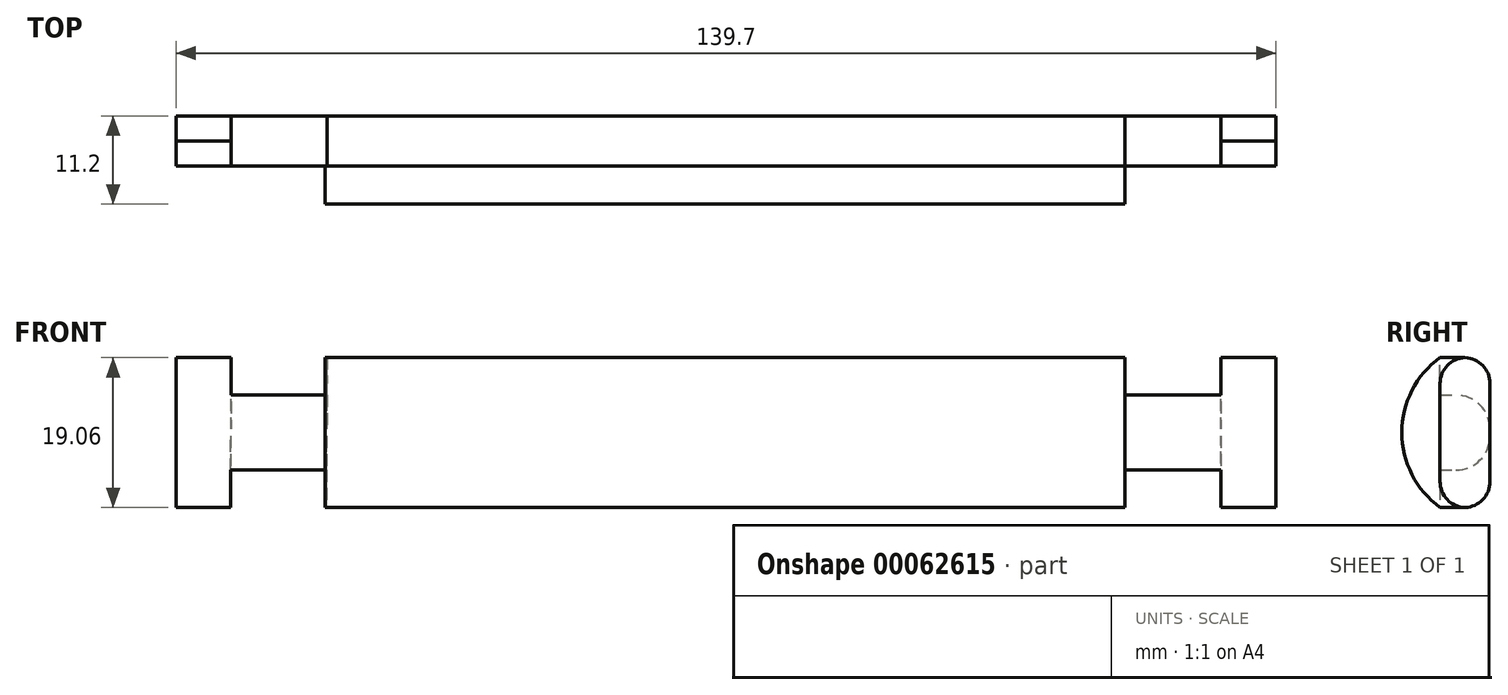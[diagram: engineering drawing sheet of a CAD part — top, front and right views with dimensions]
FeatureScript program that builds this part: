
annotation { "Feature Type Name" : "Feature", "Feature Type Description" : "" }
export const myFeature = defineFeature(function(context is Context, id is Id, definition is map)
    precondition{}
    {
        {
            var Q0;
            Q0=qCreatedBy(makeId("Front.planeOp"),FACE);
            var sketch = newSketch(context, id + "F0", { "sketchPlane" : qUnion([Q0])});
            skLineSegment(sketch, "E0.rect.bottom", {"start": v(69.85, 9.53) * mm, "end": v(-69.85, 9.53) * mm});
            skLineSegment(sketch, "E0.rect.top", {"start": v(69.85, -9.53) * mm, "end": v(-69.85, -9.53) * mm});
            skLineSegment(sketch, "E0.rect.left", {"start": v(69.85, 9.53) * mm, "end": v(69.85, -9.53) * mm});
            skLineSegment(sketch, "E0.rect.right", {"start": v(-69.85, 9.53) * mm, "end": v(-69.85, -9.53) * mm});
            skPoint(sketch, "E0.rect.middle", {"position": v(0, 0) * mm});
            skLineSegment(sketch, "E1", {"start": v(-62.88, 9.53) * mm, "end": v(-62.88, 4.76) * mm});
            skLineSegment(sketch, "E2", {"start": v(-62.88, 4.76) * mm, "end": v(-50.69, 4.76) * mm});
            skLineSegment(sketch, "E3", {"start": v(-50.69, 4.76) * mm, "end": v(-50.69, 9.53) * mm});
            skLineSegment(sketch, "E4", {"start": v(-62.92, -4.76) * mm, "end": v(-62.92, -9.53) * mm});
            skLineSegment(sketch, "E5", {"start": v(-62.92, -4.76) * mm, "end": v(-50.73, -4.76) * mm});
            skLineSegment(sketch, "E6", {"start": v(-50.73, -4.76) * mm, "end": v(-50.73, -9.53) * mm});
            skLineSegment(sketch, "E7", {"start": v(62.9, 9.53) * mm, "end": v(62.9, 4.76) * mm});
            skLineSegment(sketch, "E8", {"start": v(62.9, 4.76) * mm, "end": v(50.7, 4.76) * mm});
            skLineSegment(sketch, "E9", {"start": v(50.7, 4.76) * mm, "end": v(50.7, 9.53) * mm});
            skLineSegment(sketch, "E10", {"start": v(62.9, -9.53) * mm, "end": v(62.9, -4.76) * mm});
            skLineSegment(sketch, "E11", {"start": v(62.9, -4.76) * mm, "end": v(50.7, -4.76) * mm});
            skLineSegment(sketch, "E12", {"start": v(50.7, -4.76) * mm, "end": v(50.7, -9.53) * mm});
            skLineSegment(sketch, "E13", {"start": v(-62.88, 4.76) * mm, "end": v(-62.92, -4.76) * mm, "construction": true});
            skLineSegment(sketch, "E14", {"start": v(62.9, 4.76) * mm, "end": v(62.9, -4.76) * mm, "construction": true});
            skSolve(sketch);
        }
        {
            var Q0;
            {var subQ3=sQuery(id+"F0.wireOp",EDGE,"E0.rect.left");Q0=makeQuery(id+"F0.imprint","IMPRINT",FACE,{"disambiguationData":[TD([[makeQuery(id+"F0.imprint","IMPRINT",EDGE,{"derivedFrom":subQ3}),-1.0]])]});}
            extrude(context, id + "F1", {"entities" : qUnion([Q0]), "depth" : 6.35 * mm});
        }
        {
            var Q0;
            {var subQ0=sQuery(id+"F0.wireOp",EDGE,"E0.rect.bottom");Q0=makeQuery(id+"F1.opExtrude","CAP_EDGE",EDGE,{"disambiguationData":[OSD([subQ0]),TDD([makeQuery(id+"F0.imprint","IMPRINT",EDGE,{"disambiguationData":[TD([[makeQuery(id+"F0.imprint","INTERSECT",VERTEX,{"derivedFrom":[subQ0,sQuery(id+"F0.wireOp",EDGE,"E0.rect.left")]}),-1.0]])],"derivedFrom":subQ0})])],"isStart":true});}
            var Q1;
            {var subQ0=sQuery(id+"F0.wireOp",EDGE,"E0.rect.bottom");Q1=makeQuery(id+"F1.opExtrude","CAP_EDGE",EDGE,{"disambiguationData":[OSD([subQ0]),TDD([makeQuery(id+"F0.imprint","IMPRINT",EDGE,{"disambiguationData":[TD([[makeQuery(id+"F0.imprint","INTERSECT",VERTEX,{"derivedFrom":[subQ0,sQuery(id+"F0.wireOp",EDGE,"E3")]}),1.0]])],"derivedFrom":subQ0})])],"isStart":true});}
            var Q2;
            {var subQ0=sQuery(id+"F0.wireOp",EDGE,"E0.rect.bottom");Q2=makeQuery(id+"F1.opExtrude","CAP_EDGE",EDGE,{"disambiguationData":[OSD([subQ0]),TDD([makeQuery(id+"F0.imprint","IMPRINT",EDGE,{"disambiguationData":[TD([[makeQuery(id+"F0.imprint","INTERSECT",VERTEX,{"derivedFrom":[subQ0,sQuery(id+"F0.wireOp",EDGE,"E0.rect.right")]}),1.0]])],"derivedFrom":subQ0})])],"isStart":true});}
            var Q3;
            {var subQ0=sQuery(id+"F0.wireOp",EDGE,"E0.rect.bottom");Q3=makeQuery(id+"F1.opExtrude","CAP_EDGE",EDGE,{"disambiguationData":[OSD([subQ0]),TDD([makeQuery(id+"F0.imprint","IMPRINT",EDGE,{"disambiguationData":[TD([[makeQuery(id+"F0.imprint","INTERSECT",VERTEX,{"derivedFrom":[subQ0,sQuery(id+"F0.wireOp",EDGE,"E0.rect.right")]}),1.0]])],"derivedFrom":subQ0})])],"isStart":false});}
            var Q4;
            {var subQ0=sQuery(id+"F0.wireOp",EDGE,"E0.rect.bottom");Q4=makeQuery(id+"F1.opExtrude","CAP_EDGE",EDGE,{"disambiguationData":[OSD([subQ0]),TDD([makeQuery(id+"F0.imprint","IMPRINT",EDGE,{"disambiguationData":[TD([[makeQuery(id+"F0.imprint","INTERSECT",VERTEX,{"derivedFrom":[subQ0,sQuery(id+"F0.wireOp",EDGE,"E0.rect.left")]}),-1.0]])],"derivedFrom":subQ0})])],"isStart":false});}
            var Q5;
            {var subQ0=sQuery(id+"F0.wireOp",EDGE,"E0.rect.top");Q5=makeQuery(id+"F1.opExtrude","CAP_EDGE",EDGE,{"disambiguationData":[OSD([subQ0]),TDD([makeQuery(id+"F0.imprint","IMPRINT",EDGE,{"disambiguationData":[TD([[makeQuery(id+"F0.imprint","INTERSECT",VERTEX,{"derivedFrom":[subQ0,sQuery(id+"F0.wireOp",EDGE,"E0.rect.left")]}),-1.0]])],"derivedFrom":subQ0})])],"isStart":true});}
            var Q6;
            {var subQ0=sQuery(id+"F0.wireOp",EDGE,"E0.rect.top");Q6=makeQuery(id+"F1.opExtrude","CAP_EDGE",EDGE,{"disambiguationData":[OSD([subQ0]),TDD([makeQuery(id+"F0.imprint","IMPRINT",EDGE,{"disambiguationData":[TD([[makeQuery(id+"F0.imprint","INTERSECT",VERTEX,{"derivedFrom":[subQ0,sQuery(id+"F0.wireOp",EDGE,"E6")]}),1.0]])],"derivedFrom":subQ0})])],"isStart":true});}
            var Q7;
            {var subQ0=sQuery(id+"F0.wireOp",EDGE,"E0.rect.top");Q7=makeQuery(id+"F1.opExtrude","CAP_EDGE",EDGE,{"disambiguationData":[OSD([subQ0]),TDD([makeQuery(id+"F0.imprint","IMPRINT",EDGE,{"disambiguationData":[TD([[makeQuery(id+"F0.imprint","INTERSECT",VERTEX,{"derivedFrom":[subQ0,sQuery(id+"F0.wireOp",EDGE,"E0.rect.right")]}),1.0]])],"derivedFrom":subQ0})])],"isStart":true});}
            var Q8;
            {var subQ0=sQuery(id+"F0.wireOp",EDGE,"E0.rect.top");Q8=makeQuery(id+"F1.opExtrude","CAP_EDGE",EDGE,{"disambiguationData":[OSD([subQ0]),TDD([makeQuery(id+"F0.imprint","IMPRINT",EDGE,{"disambiguationData":[TD([[makeQuery(id+"F0.imprint","INTERSECT",VERTEX,{"derivedFrom":[subQ0,sQuery(id+"F0.wireOp",EDGE,"E0.rect.right")]}),1.0]])],"derivedFrom":subQ0})])],"isStart":false});}
            var Q9;
            {var subQ0=sQuery(id+"F0.wireOp",EDGE,"E0.rect.top");Q9=makeQuery(id+"F1.opExtrude","CAP_EDGE",EDGE,{"disambiguationData":[OSD([subQ0]),TDD([makeQuery(id+"F0.imprint","IMPRINT",EDGE,{"disambiguationData":[TD([[makeQuery(id+"F0.imprint","INTERSECT",VERTEX,{"derivedFrom":[subQ0,sQuery(id+"F0.wireOp",EDGE,"E0.rect.left")]}),-1.0]])],"derivedFrom":subQ0})])],"isStart":false});}
            fillet(context, id + "F2", {"entities" : qUnion([Q0, Q1, Q2, Q3, Q4, Q5, Q6, Q7, Q8, Q9]), "radius" : 3.3 * mm, "tangentPropagation" : true, "allowEdgeOverflow" : false});
        }
        {
            var Q0;
            Q0=makeQuery(id+"F1.opExtrude","CAP_EDGE",EDGE,{"disambiguationData":[OSD([sQuery(id+"F0.wireOp",EDGE,"E2")])],"isStart":true});
            var Q1;
            Q1=makeQuery(id+"F1.opExtrude","CAP_EDGE",EDGE,{"disambiguationData":[OSD([sQuery(id+"F0.wireOp",EDGE,"E5")])],"isStart":true});
            var Q2;
            Q2=makeQuery(id+"F1.opExtrude","CAP_EDGE",EDGE,{"disambiguationData":[OSD([sQuery(id+"F0.wireOp",EDGE,"E11")])],"isStart":true});
            var Q3;
            Q3=makeQuery(id+"F1.opExtrude","CAP_EDGE",EDGE,{"disambiguationData":[OSD([sQuery(id+"F0.wireOp",EDGE,"E8")])],"isStart":true});
            fillet(context, id + "F3", {"entities" : qUnion([Q0, Q1, Q2, Q3]), "radius" : 4.32 * mm, "tangentPropagation" : true, "allowEdgeOverflow" : false});
        }
        {
            var Q0;
            Q0=makeQuery(id+"F1.opExtrude","SWEPT_FACE",FACE,{"disambiguationData":[OSD([sQuery(id+"F0.wireOp",EDGE,"E9")])]});
            var sketch = newSketch(context, id + "F4", { "sketchPlane" : qUnion([Q0])});
            skArc(sketch, "E15", {"start": v(-6.35, 9.52) * mm, "mid": v(-11.2, 0) * mm, "end": v(-6.35, -9.51) * mm});
            skLineSegment(sketch, "E16", {"start": v(-6.35, 4.76) * mm, "end": v(-6.35, -4.82) * mm});
            skLineSegment(sketch, "E17", {"start": v(-6.35, 9.52) * mm, "end": v(-6.35, -9.51) * mm});
            skSolve(sketch);
        }
        {
            var Q0;
            {var subQ0=sQuery(id+"F4.wireOp",EDGE,"E15");Q0=makeQuery(id+"F4.imprint","IMPRINT",FACE,{"disambiguationData":[TD([[makeQuery(id+"F4.imprint","IMPRINT",EDGE,{"derivedFrom":subQ0}),1.0]])]});}
            extrude(context, id + "F5", {"entities" : qUnion([Q0]), "operationType" : NewBodyOperationType.ADD, "oppositeDirection" : true, "depth" : 101.6 * mm});
        }
    });
